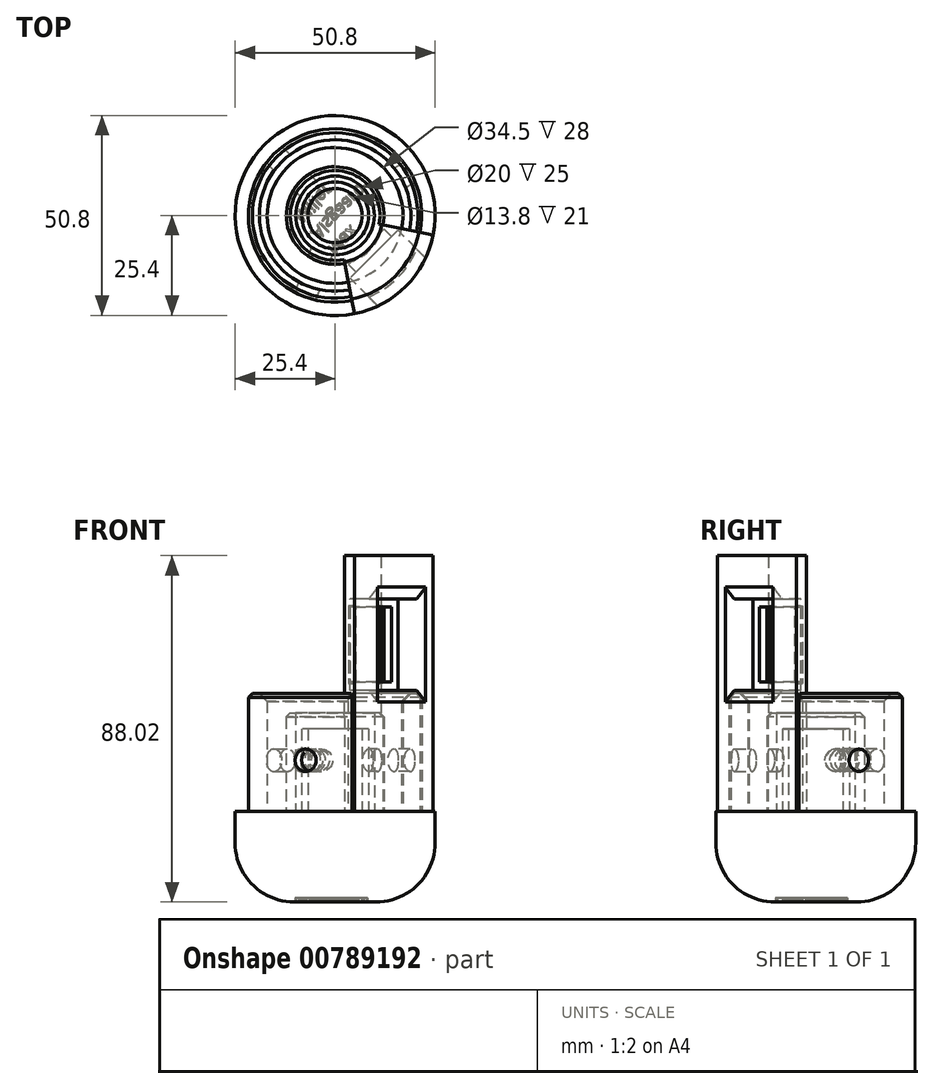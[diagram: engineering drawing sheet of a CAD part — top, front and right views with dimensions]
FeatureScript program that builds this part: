
annotation { "Feature Type Name" : "Feature", "Feature Type Description" : "" }
export const myFeature = defineFeature(function(context is Context, id is Id, definition is map)
    precondition{}
    {
        {
            var Q0;
            Q0=qCreatedBy(makeId("Right.planeOp"),FACE);
            var sketch = newSketch(context, id + "F0", { "sketchPlane" : qUnion([Q0])});
            skLineSegment(sketch, "E0", {"start": v(0, 22.52) * mm, "end": v(0, -20.14) * mm, "construction": true});
            skSolve(sketch);
        }
        {
            var Q0;
            Q0=qCreatedBy(makeId("Top.planeOp"),FACE);
            var sketch = newSketch(context, id + "F1", { "sketchPlane" : qUnion([Q0])});
            skCircle(sketch, "E1", {"center": v(0, 0) * mm, "radius": 25.4 * mm});
            skCircle(sketch, "E2", {"center": v(0, 0) * mm, "radius": 22.03 * mm});
            skCircle(sketch, "E3", {"center": v(0, 0) * mm, "radius": 17.25 * mm});
            skCircle(sketch, "E4", {"center": v(0, 0) * mm, "radius": 12.4 * mm});
            skCircle(sketch, "E5", {"center": v(0, 0) * mm, "radius": 10 * mm});
            skSolve(sketch);
        }
        {
            var Q0;
            Q0=qCreatedBy(makeId("Right.planeOp"),FACE);
            var Q1;
            Q1=sQuery(id+"F0.wireOp",EDGE,"E0");
            cPlane(context, id + "F2", {"entities" : qUnion([Q0, Q1]), "cplaneType" : CPlaneType.LINE_ANGLE, "offset" : 25 * mm, "angle" : 30 * degree, "oppositeDirection" : true, "width" : 150 * mm, "height" : 150 * mm});
        }
        {
            var Q0;
            Q0=qCreatedBy(makeId("Front.planeOp"),FACE);
            var Q1;
            Q1=sQuery(id+"F0.wireOp",EDGE,"E0");
            cPlane(context, id + "F3", {"entities" : qUnion([Q0, Q1]), "cplaneType" : CPlaneType.LINE_ANGLE, "offset" : 25 * mm, "angle" : 20 * degree, "width" : 150 * mm, "height" : 150 * mm});
        }
        {
            var Q0;
            Q0=makeQuery(id+"F1.imprint","IMPRINT",FACE,{"disambiguationData":[TD([[makeQuery(id+"F1.imprint","IMPRINT",EDGE,{"derivedFrom":sQuery(id+"F1.wireOp",EDGE,"E1")}),1.0]])]});
            var Q1;
            Q1=makeQuery(id+"F1.imprint","IMPRINT",FACE,{"disambiguationData":[TD([[makeQuery(id+"F1.imprint","IMPRINT",EDGE,{"derivedFrom":sQuery(id+"F1.wireOp",EDGE,"E2")}),1.0]])]});
            var Q2;
            Q2=makeQuery(id+"F1.imprint","IMPRINT",FACE,{"disambiguationData":[TD([[makeQuery(id+"F1.imprint","IMPRINT",EDGE,{"derivedFrom":sQuery(id+"F1.wireOp",EDGE,"E3")}),1.0]])]});
            var Q3;
            Q3=makeQuery(id+"F1.imprint","IMPRINT",FACE,{"disambiguationData":[TD([[makeQuery(id+"F1.imprint","IMPRINT",EDGE,{"derivedFrom":sQuery(id+"F1.wireOp",EDGE,"E4")}),1.0]])]});
            var Q4;
            Q4=makeQuery(id+"F1.imprint","IMPRINT",FACE,{"disambiguationData":[TD([[makeQuery(id+"F1.imprint","IMPRINT",EDGE,{"derivedFrom":sQuery(id+"F1.wireOp",EDGE,"E5")}),1.0]])]});
            extrude(context, id + "F4", {"entities" : qUnion([Q0, Q1, Q2, Q3, Q4]), "oppositeDirection" : true, "depth" : 8 * mm, "offsetDistance" : 25 * mm});
        }
        {
            var Q0;
            Q0=makeQuery(id+"F1.imprint","IMPRINT",FACE,{"disambiguationData":[TD([[makeQuery(id+"F1.imprint","IMPRINT",EDGE,{"derivedFrom":sQuery(id+"F1.wireOp",EDGE,"E2")}),1.0]])]});
            extrude(context, id + "F5", {"entities" : qUnion([Q0]), "operationType" : NewBodyOperationType.ADD, "depth" : 30 * mm, "offsetDistance" : 25 * mm});
        }
        {
            var Q0;
            Q0=makeQuery(id+"F1.imprint","IMPRINT",FACE,{"disambiguationData":[TD([[makeQuery(id+"F1.imprint","IMPRINT",EDGE,{"derivedFrom":sQuery(id+"F1.wireOp",EDGE,"E4")}),1.0]])]});
            extrude(context, id + "F6", {"entities" : qUnion([Q0]), "operationType" : NewBodyOperationType.ADD, "depth" : 25 * mm, "offsetDistance" : 25 * mm});
        }
        {
            var Q0;
            Q0=qCreatedBy(id+"F2.planeOp",FACE);
            var sketch = newSketch(context, id + "F7", { "sketchPlane" : qUnion([Q0])});
            skCircle(sketch, "E6", {"center": v(0, 13) * mm, "radius": 2.85 * mm});
            skSolve(sketch);
        }
        {
            var Q0;
            Q0=qCreatedBy(id+"F3.planeOp",FACE);
            var sketch = newSketch(context, id + "F8", { "sketchPlane" : qUnion([Q0])});
            skCircle(sketch, "E7", {"center": v(0, 13) * mm, "radius": 2.85 * mm});
            skLineSegment(sketch, "E8", {"start": v(0, -1.69) * mm, "end": v(0, 3.4) * mm, "construction": true});
            skSolve(sketch);
        }
        {
            var Q0;
            Q0=qSketchRegion(id+"F8",true);
            extrude(context, id + "F9", {"entities" : qUnion([Q0]), "operationType" : NewBodyOperationType.REMOVE, "oppositeDirection" : true, "depth" : 25 * mm, "offsetDistance" : 25 * mm, "hasSecondDirection" : true, "secondDirectionOppositeDirection" : false, "secondDirectionDepth" : 0 * mm});
        }
        {
            var Q0;
            Q0=qSketchRegion(id+"F7",true);
            var Q1;
            Q1=sQuery(id+"F7.wireOp",EDGE,"E6");
            extrude(context, id + "F10", {"entities" : qUnion([Q0]), "operationType" : NewBodyOperationType.REMOVE, "surfaceEntities" : qUnion([Q1]), "depth" : 0 * mm, "offsetDistance" : 25 * mm, "hasSecondDirection" : true, "secondDirectionOppositeDirection" : true, "secondDirectionDepth" : 25 * mm});
        }
        {
            var Q0;
            Q0=qCreatedBy(makeId("Front.planeOp"),FACE);
            var Q1;
            Q1=qCreatedBy(makeId("Right.planeOp"),FACE);
            cPlane(context, id + "F11", {"entities" : qUnion([Q0, Q1]), "cplaneType" : CPlaneType.MID_PLANE, "offset" : 25 * mm, "width" : 150 * mm, "height" : 150 * mm});
        }
        {
            var Q0;
            Q0=qCreatedBy(id+"F11.planeOp",FACE);
            var sketch = newSketch(context, id + "F12", { "sketchPlane" : qUnion([Q0])});
            skLineSegment(sketch, "E9", {"start": v(21.68, 65) * mm, "end": v(21.68, 0) * mm});
            skLineSegment(sketch, "E10", {"start": v(21.68, 0) * mm, "end": v(25.41, 0) * mm});
            skLineSegment(sketch, "E11", {"start": v(25.41, 0) * mm, "end": v(25.41, 65) * mm});
            skLineSegment(sketch, "E12", {"start": v(25.41, 65) * mm, "end": v(21.68, 65) * mm});
            skLineSegment(sketch, "E13.bottom", {"start": v(21.68, 0.02) * mm, "end": v(12.08, 0.02) * mm});
            skLineSegment(sketch, "E13.top", {"start": v(21.68, 65.02) * mm, "end": v(12.08, 65.02) * mm});
            skLineSegment(sketch, "E13.left", {"start": v(21.68, 0.02) * mm, "end": v(21.68, 65.02) * mm});
            skLineSegment(sketch, "E13.right", {"start": v(12.08, 0.02) * mm, "end": v(12.08, 65.02) * mm});
            skSolve(sketch);
        }
        {
            var Q0;
            {var subQ1=sQuery(id+"F12.wireOp",EDGE,"E9");Q0=makeQuery(id+"F12.imprint","IMPRINT",FACE,{"disambiguationData":[TD([[makeQuery(id+"F12.imprint","IMPRINT",EDGE,{"derivedFrom":subQ1}),1.0]])]});}
            var Q1;
            {var subQ3=sQuery(id+"F12.wireOp",EDGE,"E13.bottom");Q1=makeQuery(id+"F12.imprint","IMPRINT",FACE,{"disambiguationData":[TD([[makeQuery(id+"F12.imprint","IMPRINT",EDGE,{"derivedFrom":subQ3}),-1.0]])]});}
            var Q2;
            Q2=sQuery(id+"F8.wireOp",EDGE,"E8");
            revolve(context, id + "F13", {"operationType" : NewBodyOperationType.ADD, "surfaceOperationType" : NewSurfaceOperationType.NEW, "entities" : qUnion([Q0, Q1]), "axis" : qUnion([Q2]), "revolveType" : RevolveType.SYMMETRIC, "angle" : 67.67 * degree});
        }
        {
            var Q0;
            Q0=qCreatedBy(id+"F11.planeOp",FACE);
            var sketch = newSketch(context, id + "F14", { "sketchPlane" : qUnion([Q0])});
            skLineSegment(sketch, "E14.bottom", {"start": v(25.41, 30.8) * mm, "end": v(13.91, 30.8) * mm});
            skLineSegment(sketch, "E14.top", {"start": v(25.41, 54) * mm, "end": v(13.91, 54) * mm});
            skLineSegment(sketch, "E14.left", {"start": v(25.41, 30.8) * mm, "end": v(25.41, 54) * mm});
            skLineSegment(sketch, "E14.right", {"start": v(13.91, 30.8) * mm, "end": v(13.91, 54) * mm});
            skLineSegment(sketch, "E15", {"start": v(25.41, 65) * mm, "end": v(25.41, 0) * mm});
            skLineSegment(sketch, "E16", {"start": v(25.41, 65) * mm, "end": v(25.41, 0) * mm, "construction": true});
            skSolve(sketch);
        }
        {
            var Q0;
            Q0=qSketchRegion(id+"F14",true);
            extrude(context, id + "F15", {"entities" : qUnion([Q0]), "operationType" : NewBodyOperationType.REMOVE, "oppositeDirection" : true, "depth" : 8.6 * mm, "offsetDistance" : 25 * mm, "hasSecondDirection" : true, "secondDirectionOppositeDirection" : false, "secondDirectionDepth" : 8.6 * mm});
        }
        {
            var Q0;
            Q0=qCreatedBy(makeId("Right.planeOp"),FACE);
            var Q1;
            Q1=qCreatedBy(makeId("Front.planeOp"),FACE);
            cPlane(context, id + "F16", {"entities" : qUnion([Q0, Q1]), "cplaneType" : CPlaneType.MID_PLANE, "offset" : 25 * mm, "flipAlignment" : true, "width" : 150 * mm, "height" : 150 * mm});
        }
        {
            var Q0;
            Q0=qCreatedBy(id+"F16.planeOp",FACE);
            cPlane(context, id + "F17", {"entities" : qUnion([Q0]), "cplaneType" : CPlaneType.OFFSET, "offset" : 25.4 * mm, "width" : 150 * mm, "height" : 150 * mm});
        }
        {
            var Q0;
            Q0=qCreatedBy(id+"F11.planeOp",FACE);
            var sketch = newSketch(context, id + "F18", { "sketchPlane" : qUnion([Q0])});
            skLineSegment(sketch, "E17.0", {"start": v(13.91, 30.8) * mm, "end": v(13.91, 54) * mm});
            skLineSegment(sketch, "E18.0", {"start": v(25.41, 54) * mm, "end": v(13.91, 54) * mm});
            skLineSegment(sketch, "E19.0", {"start": v(25.41, 30.8) * mm, "end": v(13.91, 30.8) * mm});
            skLineSegment(sketch, "E20.bottom", {"start": v(13.91, 51.9) * mm, "end": v(11.22, 51.9) * mm});
            skLineSegment(sketch, "E20.top", {"start": v(13.91, 32.9) * mm, "end": v(11.22, 32.9) * mm});
            skLineSegment(sketch, "E20.left", {"start": v(13.91, 51.9) * mm, "end": v(13.91, 32.9) * mm});
            skLineSegment(sketch, "E20.right", {"start": v(11.22, 51.9) * mm, "end": v(11.22, 32.9) * mm});
            skSolve(sketch);
        }
        {
            var Q0;
            Q0=makeQuery(id+"F18.imprint","IMPRINT",FACE,{"disambiguationData":[TD([[makeQuery(id+"F18.imprint","IMPRINT",EDGE,{"derivedFrom":sQuery(id+"F18.wireOp",EDGE,"E20.bottom")}),1.0]])]});
            extrude(context, id + "F19", {"entities" : qUnion([Q0]), "operationType" : NewBodyOperationType.REMOVE, "endBound" : BoundingType.SYMMETRIC, "oppositeDirection" : true, "depth" : 12.68 * mm, "offsetDistance" : 25 * mm});
        }
        {
            var Q0;
            Q0=qCreatedBy(id+"F11.planeOp",FACE);
            var sketch = newSketch(context, id + "F20", { "sketchPlane" : qUnion([Q0])});
            skLineSegment(sketch, "E21.0.0", {"start": v(25.41, 30.8) * mm, "end": v(25.41, 54) * mm});
            skLineSegment(sketch, "E21.0.1", {"start": v(25.41, 54) * mm, "end": v(13.91, 54) * mm});
            skLineSegment(sketch, "E21.0.2", {"start": v(13.91, 54) * mm, "end": v(13.91, 30.8) * mm});
            skLineSegment(sketch, "E21.0.3", {"start": v(13.91, 30.8) * mm, "end": v(25.41, 30.8) * mm});
            skLineSegment(sketch, "E22.0.0", {"start": v(13.91, 32.9) * mm, "end": v(13.91, 51.9) * mm});
            skLineSegment(sketch, "E22.0.1", {"start": v(13.91, 51.9) * mm, "end": v(11.22, 51.9) * mm});
            skLineSegment(sketch, "E22.0.2", {"start": v(11.22, 51.9) * mm, "end": v(11.22, 32.9) * mm});
            skLineSegment(sketch, "E22.0.3", {"start": v(11.22, 32.9) * mm, "end": v(13.91, 32.9) * mm});
            skLineSegment(sketch, "E23", {"start": v(11.22, 42.4) * mm, "end": v(3.36, 42.4) * mm, "construction": true});
            skLineSegment(sketch, "E24.bottom", {"start": v(11.22, 52.25) * mm, "end": v(8.97, 52.25) * mm});
            skLineSegment(sketch, "E24.top", {"start": v(11.22, 32.55) * mm, "end": v(8.97, 32.55) * mm});
            skLineSegment(sketch, "E24.left", {"start": v(11.22, 52.25) * mm, "end": v(11.22, 32.55) * mm});
            skLineSegment(sketch, "E24.right", {"start": v(8.97, 52.25) * mm, "end": v(8.97, 32.55) * mm});
            skPoint(sketch, "E24.middle", {"position": v(10.1, 42.4) * mm});
            skSolve(sketch);
        }
        {
            var Q0;
            {var subQ3=sQuery(id+"F20.wireOp",EDGE,"E24.bottom");Q0=makeQuery(id+"F20.imprint","IMPRINT",FACE,{"disambiguationData":[TD([[makeQuery(id+"F20.imprint","IMPRINT",EDGE,{"derivedFrom":subQ3}),1.0]])]});}
            extrude(context, id + "F21", {"entities" : qUnion([Q0]), "operationType" : NewBodyOperationType.REMOVE, "endBound" : BoundingType.SYMMETRIC, "oppositeDirection" : true, "depth" : 11.6 * mm, "offsetDistance" : 25 * mm});
        }
        {
            var Q0;
            Q0=makeQuery(id+"F4.opExtrude","CAP_FACE",FACE,{"disambiguationData":[OSD([sQuery(id+"F1.wireOp",EDGE,"E1")])],"isStart":false});
            cPlane(context, id + "F22", {"entities" : qUnion([Q0]), "cplaneType" : CPlaneType.OFFSET, "offset" : 0 * mm, "width" : 150 * mm, "height" : 150 * mm});
        }
        {
            var Q0;
            Q0=qCreatedBy(id+"F22.planeOp",FACE);
            var sketch = newSketch(context, id + "F23", { "sketchPlane" : qUnion([Q0])});
            skCircle(sketch, "E25.0.0", {"center": v(0, 0) * mm, "radius": 25.4 * mm});
            skSolve(sketch);
        }
        {
            var Q0;
            Q0=makeQuery(id+"F23.imprint","IMPRINT",FACE,{"disambiguationData":[TD([[makeQuery(id+"F23.imprint","IMPRINT",EDGE,{"derivedFrom":sQuery(id+"F23.wireOp",EDGE,"E25.0.0")}),1.0]])]});
            extrude(context, id + "F24", {"entities" : qUnion([Q0]), "operationType" : NewBodyOperationType.ADD, "surfaceOperationType" : NewSurfaceOperationType.ADD, "depth" : 15 * mm, "offsetDistance" : 25 * mm});
        }
        {
            var Q0;
            Q0=makeQuery(id+"F24.opExtrude","CAP_EDGE",EDGE,{"disambiguationData":[OSD([sQuery(id+"F23.wireOp",EDGE,"E25.0.0")])],"isStart":false});
            fillet(context, id + "F25", {"entities" : qUnion([Q0]), "radius" : 15 * mm, "tangentPropagation" : true, "allowEdgeOverflow" : false});
        }
        {
            var Q0;
            Q0=qCreatedBy(id+"F22.planeOp",FACE);
            cPlane(context, id + "F26", {"entities" : qUnion([Q0]), "cplaneType" : CPlaneType.OFFSET, "offset" : 15 * mm, "width" : 150 * mm, "height" : 150 * mm});
        }
        {
            var Q0;
            Q0=qCreatedBy(id+"F26.planeOp",FACE);
            var sketch = newSketch(context, id + "F27", { "sketchPlane" : qUnion([Q0])});
            skText(sketch, "E26", { "text": "Max\nAlsgaard\nMiller", "fontName": "OpenSans-Regular.ttf"});
            const initialGuessF27  = {"E26": [-0.0021, 0.00836, 0.7071, -0.7071, 0.00315]};
            skSetInitialGuess(sketch, initialGuessF27);
            skSolve(sketch);
        }
        {
            var Q0;
            Q0=qSketchRegion(id+"F27",true);
            extrude(context, id + "F28", {"entities" : qUnion([Q0]), "operationType" : NewBodyOperationType.REMOVE, "oppositeDirection" : true, "depth" : 1 * mm, "offsetDistance" : 25 * mm});
        }
        {
            var Q0;
            Q0=qCreatedBy(makeId("Top.planeOp"),FACE);
            var sketch = newSketch(context, id + "F29", { "sketchPlane" : qUnion([Q0])});
            skCircle(sketch, "E27", {"center": v(0, 0) * mm, "radius": 6.9 * mm});
            skCircle(sketch, "E28", {"center": v(0, 0) * mm, "radius": 8.5 * mm});
            skSolve(sketch);
        }
        {
            var Q0;
            Q0=makeQuery(id+"F29.imprint","IMPRINT",FACE,{"disambiguationData":[TD([[makeQuery(id+"F29.imprint","IMPRINT",EDGE,{"derivedFrom":sQuery(id+"F29.wireOp",EDGE,"E27")}),-1.0]])]});
            extrude(context, id + "F30", {"entities" : qUnion([Q0]), "operationType" : NewBodyOperationType.ADD, "depth" : 21 * mm, "offsetDistance" : 25 * mm});
        }
        {
            var Q0;
            Q0=qCreatedBy(id+"F16.planeOp",FACE);
            var sketch = newSketch(context, id + "F31", { "sketchPlane" : qUnion([Q0])});
            skLineSegment(sketch, "E29.0", {"start": v(-25.4, 0) * mm, "end": v(25.4, 0) * mm});
            skCircle(sketch, "E30", {"center": v(0, 13) * mm, "radius": 2.85 * mm});
            skSolve(sketch);
        }
        {
            var Q0;
            Q0=qSketchRegion(id+"F31",true);
            extrude(context, id + "F32", {"entities" : qUnion([Q0]), "operationType" : NewBodyOperationType.REMOVE, "oppositeDirection" : true, "depth" : 25 * mm, "offsetDistance" : 25 * mm});
        }
        {
            var Q0;
            Q0=makeQuery(id+"F5.opExtrude","CAP_EDGE",EDGE,{"disambiguationData":[OSD([sQuery(id+"F1.wireOp",EDGE,"E3")])],"isStart":false});
            chamfer(context, id + "F33", {"entities" : qUnion([Q0]), "width" : 2 * mm, "tangentPropagation" : true});
        }
        {
            var Q0;
            Q0=makeQuery(id+"F6.opExtrude","CAP_EDGE",EDGE,{"disambiguationData":[OSD([sQuery(id+"F1.wireOp",EDGE,"E4")])],"isStart":false});
            chamfer(context, id + "F34", {"entities" : qUnion([Q0]), "width" : 1 * mm, "tangentPropagation" : true});
        }
        {
            var Q0;
            Q0=makeQuery(id+"F5.opExtrude","CAP_EDGE",EDGE,{"disambiguationData":[OSD([sQuery(id+"F1.wireOp",EDGE,"E2")])],"isStart":false});
            chamfer(context, id + "F35", {"entities" : qUnion([Q0]), "width" : 1 * mm, "tangentPropagation" : true});
        }
        {
            var Q0;
            Q0=makeQuery(id+"F15.boolean.opBoolean","INTERSECT",EDGE,{"derivedFrom":[makeQuery(id+"F13.opRevolve","SWEPT_FACE",FACE,{"disambiguationData":[OSD([sQuery(id+"F12.wireOp",EDGE,"E11")])]}),makeQuery(id+"F15.opExtrude","SWEPT_FACE",FACE,{"disambiguationData":[OSD([sQuery(id+"F14.wireOp",EDGE,"E14.top")])]})]});
            var Q1;
            Q1=makeQuery(id+"F15.boolean.opBoolean","INTERSECT",EDGE,{"derivedFrom":[makeQuery(id+"F13.opRevolve","SWEPT_FACE",FACE,{"disambiguationData":[OSD([sQuery(id+"F12.wireOp",EDGE,"E11")])]}),makeQuery(id+"F15.opExtrude","SWEPT_FACE",FACE,{"disambiguationData":[OSD([sQuery(id+"F14.wireOp",EDGE,"E14.bottom")])]})]});
            chamfer(context, id + "F36", {"entities" : qUnion([Q0, Q1]), "width" : 3 * mm, "tangentPropagation" : true});
        }
    });
